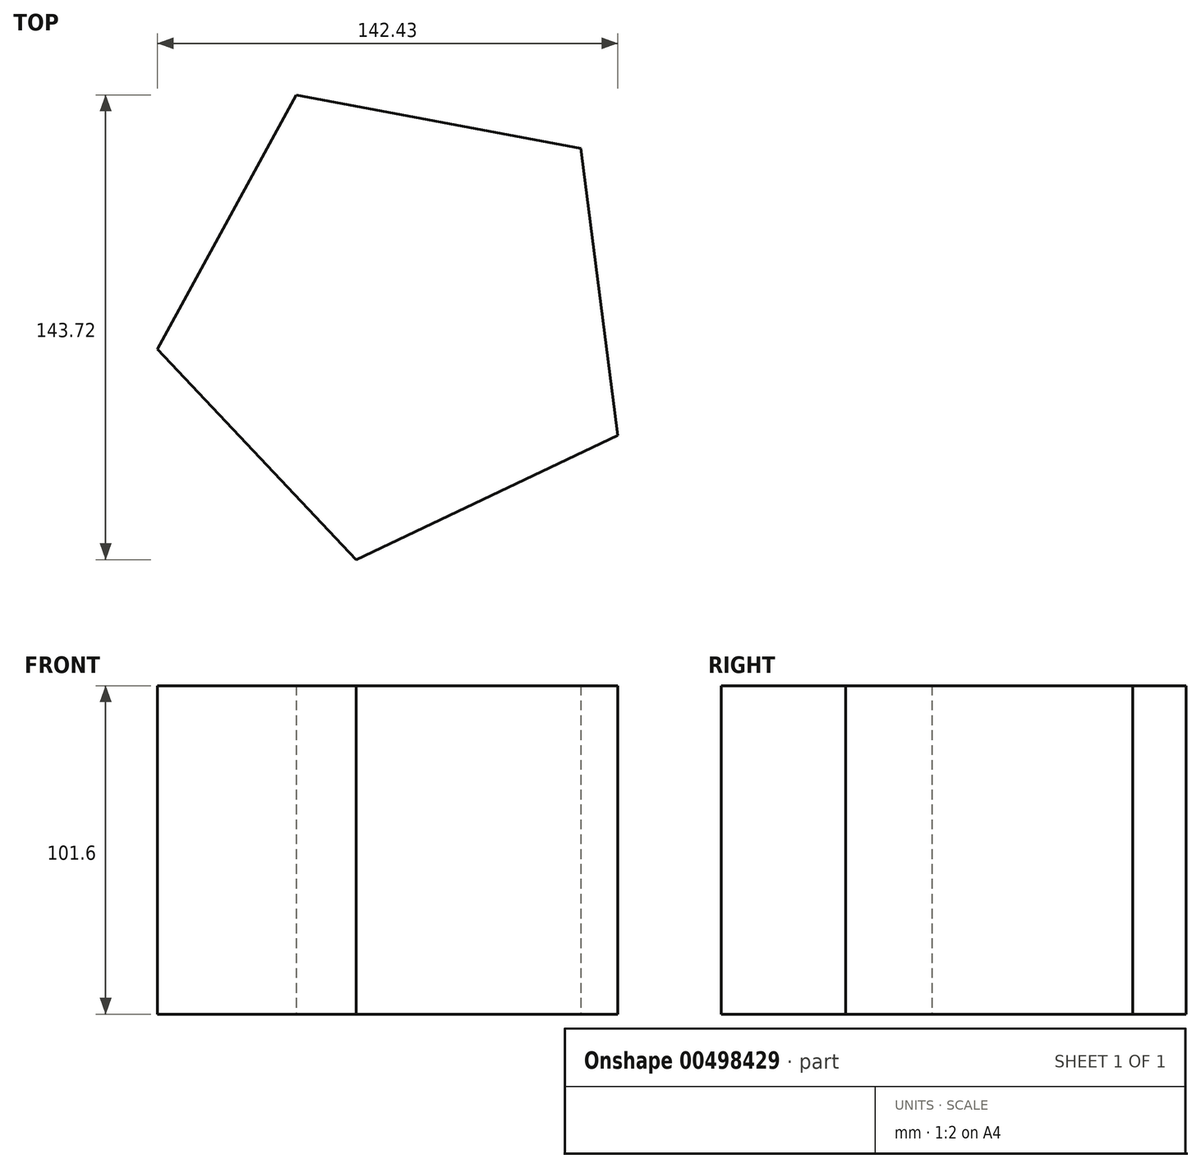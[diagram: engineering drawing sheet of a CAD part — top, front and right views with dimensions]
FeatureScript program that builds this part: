
annotation { "Feature Type Name" : "Feature", "Feature Type Description" : "" }
export const myFeature = defineFeature(function(context is Context, id is Id, definition is map)
    precondition{}
    {
        {
            var Q0;
            Q0=qCreatedBy(makeId("Top.planeOp"),FACE);
            var sketch = newSketch(context, id + "F0", { "sketchPlane" : qUnion([Q0])});
            skCircle(sketch, "E0.cCircle", {"center": v(0, 0) * mm, "radius": 76.19 * mm, "construction": true});
            skLineSegment(sketch, "E0.0", {"start": v(55.38, 52.32) * mm, "end": v(66.87, -36.5) * mm});
            skLineSegment(sketch, "E0.1", {"start": v(66.87, -36.5) * mm, "end": v(-14.05, -74.88) * mm});
            skLineSegment(sketch, "E0.2", {"start": v(-14.05, -74.88) * mm, "end": v(-75.56, -9.78) * mm});
            skLineSegment(sketch, "E0.3", {"start": v(-75.56, -9.78) * mm, "end": v(-32.65, 68.84) * mm});
            skLineSegment(sketch, "E0.4", {"start": v(-32.65, 68.84) * mm, "end": v(55.38, 52.32) * mm});
            skSolve(sketch);
        }
        {
            var Q0;
            Q0 = qSketchRegion(id + "F0", true);
            var Q1;
            Q1=makeQuery(id+"F0.imprint","IMPRINT",FACE,{"disambiguationData":[TD([[makeQuery(id+"F0.imprint","IMPRINT",EDGE,{"derivedFrom":sQuery(id+"F0.wireOp",EDGE,"E0.0")}),-1.0]])]});
            extrude(context, id + "F1", {"entities" : qUnion([Q0, Q1]), "depth" : 101.6 * mm, "offsetDistance" : 25.4 * mm});
        }
    });
